# Revit family: Faucet-Wall_Mount-Lavatory-KOHLER-PARALLEL-K-22569T
name_source: partatom
category: Plumbing Fixtures
revit_build: Autodesk Revit 2017 (Build: 20160225_1515(x64)
units: mm (PartAtom-declared; Revit-internal decimal feet)

## family parameters
Cut with Voids When Loaded = No
Host = Face
OmniClass Number = 23.31.11.00
OmniClass Title = Faucets
Part Type = Normal
Room Calculation Point = No
Round Connector Dimension = Use Diameter
Shared = No

## types (4) — shared parameters
ADA Compliant = No
Assembly Code = D2010
CW Connection = Yes
Cold Water Inlet = Cold Water Inlet
Date Modified = 05/13/2020
Default Elevation = 36"
Description = Double-handle faucet for wall outlet outlet spout length 168mm
Drain Included = Yes
Flow Rate = 0 GPM
HW Connection = Yes
Handle Clearance = 2 7/16"
Height = 2"
Hot Water Inlet = Hot Water Inlet
Length = 6 5/8"
Manufacturer = KOHLER Co.
MasterFormat 1995 = 15410
MasterFormat 2004 = 22.41.39
Material = Premium Metal Construction
Pressure = 116.03 psi
Product Documentation Link = http://files.kohler.com.cn
Product Name = PARALLEL
Product Page URL = http://www.kohler.com.cn
Spout Reach = 6 5/8"
URL = http://www.kohler.com.cn
Vent Connection = No
Waste Connection = No
Waste Water Outlet = Waste Water Outlet
WaterSense Certified = No

## per-type parameters (varying)
| type | Finish | Model | Type |
| BN-Roman Silver | Kohler-Metal-BN-Roman_Silver | K-22569T-4-BN | 2 |
| RGD-Rose Gold | Kohler-Metal-RGD-Polished_Rose_Gold | K-22569T-4-RGD | 3 |
| AF-Flange Gold | Kohler-Metal-AF-Flange_Gold | K-22569T-4-AF | 4 |
| CP-Polished Chrome | Kohler-Metal-CP-Polished_Chrome | K-22569T-4-CP | 1 |

## geometry (parser evidence)
native form markers: Sweep x9
no freeform markers — native parametric forms only
